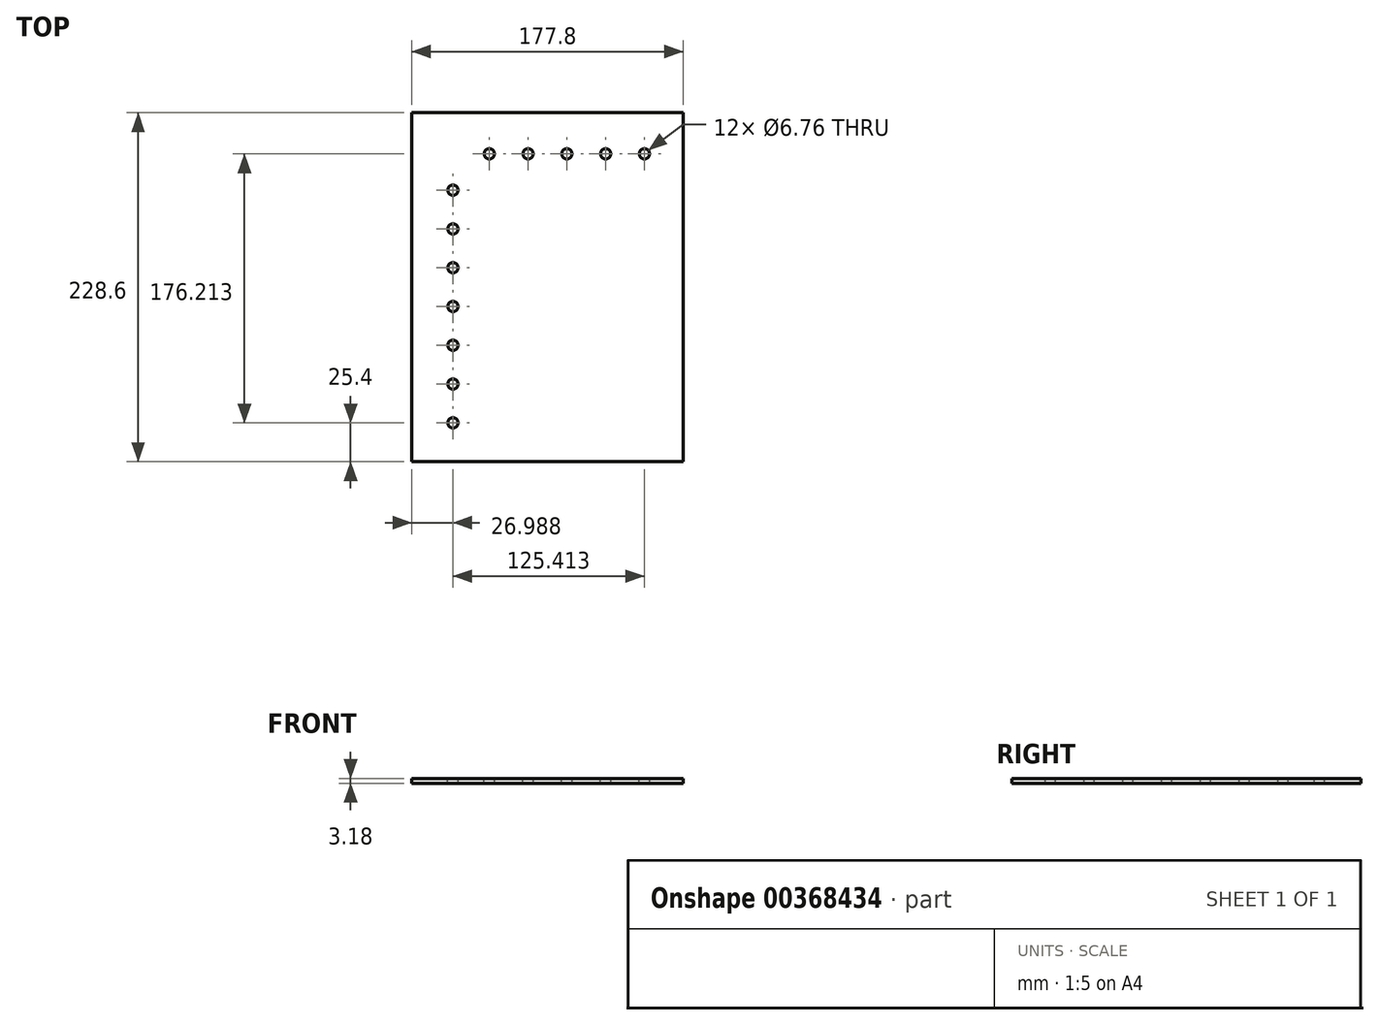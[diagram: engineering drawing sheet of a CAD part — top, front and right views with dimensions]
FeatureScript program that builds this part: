
annotation { "Feature Type Name" : "Feature", "Feature Type Description" : "" }
export const myFeature = defineFeature(function(context is Context, id is Id, definition is map)
    precondition{}
    {
        {
            var Q0;
            Q0=qCreatedBy(makeId("Top.planeOp"),FACE);
            var sketch = newSketch(context, id + "F0", { "sketchPlane" : qUnion([Q0])});
            skLineSegment(sketch, "E0.bottom", {"start": v(0, 0) * mm, "end": v(50.8, 0) * mm});
            skLineSegment(sketch, "E0.top", {"start": v(0, 177.8) * mm, "end": v(50.8, 177.8) * mm});
            skLineSegment(sketch, "E0.left", {"start": v(0, 0) * mm, "end": v(0, 177.8) * mm});
            skLineSegment(sketch, "E0.right", {"start": v(50.8, 0) * mm, "end": v(50.8, 177.8) * mm});
            skLineSegment(sketch, "E1.bottom", {"start": v(0, 228.6) * mm, "end": v(177.8, 228.6) * mm});
            skLineSegment(sketch, "E1.top", {"start": v(0, 177.8) * mm, "end": v(177.8, 177.8) * mm});
            skLineSegment(sketch, "E1.left", {"start": v(0, 228.6) * mm, "end": v(0, 177.8) * mm});
            skLineSegment(sketch, "E1.right", {"start": v(177.8, 228.6) * mm, "end": v(177.8, 177.8) * mm});
            skSolve(sketch);
        }
        {
            var Q0;
            Q0=makeQuery(id+"F0.imprint","IMPRINT",FACE,{"disambiguationData":[TD([[makeQuery(id+"F0.imprint","IMPRINT",EDGE,{"derivedFrom":sQuery(id+"F0.wireOp",EDGE,"E1.bottom")}),-1.0]])]});
            var Q1;
            Q1=makeQuery(id+"F0.imprint","IMPRINT",FACE,{"disambiguationData":[TD([[makeQuery(id+"F0.imprint","IMPRINT",EDGE,{"derivedFrom":sQuery(id+"F0.wireOp",EDGE,"E0.bottom")}),1.0]])]});
            extrude(context, id + "F1", {"entities" : qUnion([Q0, Q1]), "depth" : 3.17 * mm});
        }
        {
            var Q0;
            Q0=makeQuery(id+"F1.opExtrude","CAP_FACE",FACE,{"disambiguationData":[OSD([sQuery(id+"F0.wireOp",EDGE,"E0.bottom"),sQuery(id+"F0.wireOp",EDGE,"E0.left"),sQuery(id+"F0.wireOp",EDGE,"E0.right"),sQuery(id+"F0.wireOp",EDGE,"E1.bottom"),sQuery(id+"F0.wireOp",EDGE,"E1.top"),sQuery(id+"F0.wireOp",EDGE,"E1.left"),sQuery(id+"F0.wireOp",EDGE,"E1.right")])],"isStart":false});
            var sketch = newSketch(context, id + "F2", { "sketchPlane" : qUnion([Q0])});
            skLineSegment(sketch, "E2.0.0", {"start": v(177.8, 228.6) * mm, "end": v(0, 228.6) * mm, "construction": true});
            skLineSegment(sketch, "E2.0.1", {"start": v(0, 228.6) * mm, "end": v(0, 0) * mm, "construction": true});
            skLineSegment(sketch, "E2.0.2", {"start": v(0, 0) * mm, "end": v(50.8, 0) * mm, "construction": true});
            skLineSegment(sketch, "E2.0.3", {"start": v(50.8, 0) * mm, "end": v(50.8, 177.8) * mm, "construction": true});
            skLineSegment(sketch, "E2.0.4", {"start": v(50.8, 177.8) * mm, "end": v(177.8, 177.8) * mm, "construction": true});
            skLineSegment(sketch, "E2.0.5", {"start": v(177.8, 177.8) * mm, "end": v(177.8, 228.6) * mm, "construction": true});
            skLineSegment(sketch, "E3.0", {"start": v(3.18, 225.43) * mm, "end": v(3.18, 0) * mm});
            skLineSegment(sketch, "E4.0", {"start": v(177.8, 225.43) * mm, "end": v(3.17, 225.43) * mm});
            skLineSegment(sketch, "E5", {"start": v(177.8, 225.43) * mm, "end": v(177.8, 228.6) * mm});
            skLineSegment(sketch, "E6", {"start": v(177.8, 228.6) * mm, "end": v(0, 228.6) * mm});
            skLineSegment(sketch, "E7", {"start": v(0, 228.6) * mm, "end": v(0, 0) * mm});
            skLineSegment(sketch, "E8", {"start": v(0, 0) * mm, "end": v(3.18, 0) * mm});
            skSolve(sketch);
        }
        {
            var Q0;
            Q0=makeQuery(id+"F2.imprint","IMPRINT",FACE,{"disambiguationData":[TD([[makeQuery(id+"F2.imprint","IMPRINT",EDGE,{"derivedFrom":sQuery(id+"F2.wireOp",EDGE,"E3.0")}),-1.0]])]});
            extrude(context, id + "F3", {"entities" : qUnion([Q0]), "operationType" : NewBodyOperationType.ADD, "depth" : 76.2 * mm});
        }
        {
            var Q0;
            Q0=makeQuery(id+"F3.opExtrude","CAP_FACE",FACE,{"disambiguationData":[OSD([sQuery(id+"F2.wireOp",EDGE,"E3.0"),sQuery(id+"F2.wireOp",EDGE,"E4.0"),sQuery(id+"F2.wireOp",EDGE,"E5"),sQuery(id+"F2.wireOp",EDGE,"E6"),sQuery(id+"F2.wireOp",EDGE,"E7"),sQuery(id+"F2.wireOp",EDGE,"E8")])],"isStart":false});
            var sketch = newSketch(context, id + "F4", { "sketchPlane" : qUnion([Q0])});
            skLineSegment(sketch, "E9.0.0", {"start": v(0, 228.6) * mm, "end": v(177.8, 228.6) * mm});
            skLineSegment(sketch, "E9.0.1", {"start": v(177.8, 228.6) * mm, "end": v(177.8, 177.8) * mm});
            skLineSegment(sketch, "E9.0.2", {"start": v(177.8, 177.8) * mm, "end": v(50.8, 177.8) * mm});
            skLineSegment(sketch, "E9.0.3", {"start": v(50.8, 177.8) * mm, "end": v(50.8, 0) * mm});
            skLineSegment(sketch, "E9.0.4", {"start": v(50.8, 0) * mm, "end": v(0, 0) * mm});
            skLineSegment(sketch, "E9.0.5", {"start": v(0, 0) * mm, "end": v(0, 228.6) * mm});
            skSolve(sketch);
        }
        {
            var Q0;
            {var subQ4=sQuery(id+"F4.wireOp",EDGE,"E9.0.0");Q0=makeQuery(id+"F4.imprint","IMPRINT",FACE,{"disambiguationData":[TD([[makeQuery(id+"F4.imprint","IMPRINT",EDGE,{"derivedFrom":subQ4}),-1.0]])]});}
            var Q1;
            {var subQ3=sQuery(id+"F4.wireOp",EDGE,"E9.0.2");Q1=makeQuery(id+"F4.imprint","IMPRINT",FACE,{"disambiguationData":[TD([[makeQuery(id+"F4.imprint","IMPRINT",EDGE,{"derivedFrom":subQ3}),-1.0]])]});}
            extrude(context, id + "F5", {"entities" : qUnion([Q0, Q1]), "operationType" : NewBodyOperationType.ADD, "depth" : 3.17 * mm});
        }
        {
            var Q0;
            Q0=makeQuery(id+"F5.opExtrude","CAP_FACE",FACE,{"disambiguationData":[OSD([sQuery(id+"F4.wireOp",EDGE,"E9.0.0"),sQuery(id+"F4.wireOp",EDGE,"E9.0.1"),sQuery(id+"F4.wireOp",EDGE,"E9.0.2"),sQuery(id+"F4.wireOp",EDGE,"E9.0.3"),sQuery(id+"F4.wireOp",EDGE,"E9.0.4"),sQuery(id+"F4.wireOp",EDGE,"E9.0.5")])],"isStart":false});
            var sketch = newSketch(context, id + "F6", { "sketchPlane" : qUnion([Q0])});
            skLineSegment(sketch, "E10.0.0", {"start": v(50.8, 177.8) * mm, "end": v(177.8, 177.8) * mm, "construction": true});
            skLineSegment(sketch, "E10.0.1", {"start": v(177.8, 177.8) * mm, "end": v(177.8, 228.6) * mm, "construction": true});
            skLineSegment(sketch, "E10.0.2", {"start": v(177.8, 228.6) * mm, "end": v(0, 228.6) * mm, "construction": true});
            skLineSegment(sketch, "E10.0.3", {"start": v(0, 228.6) * mm, "end": v(0, 0) * mm, "construction": true});
            skLineSegment(sketch, "E10.0.4", {"start": v(0, 0) * mm, "end": v(50.8, 0) * mm, "construction": true});
            skLineSegment(sketch, "E10.0.5", {"start": v(50.8, 0) * mm, "end": v(50.8, 177.8) * mm, "construction": true});
            skLineSegment(sketch, "E11.0.0", {"start": v(177.8, 177.8) * mm, "end": v(177.8, 225.43) * mm, "construction": true});
            skLineSegment(sketch, "E11.0.1", {"start": v(177.8, 225.43) * mm, "end": v(3.17, 225.43) * mm, "construction": true});
            skLineSegment(sketch, "E11.0.2", {"start": v(3.18, 225.43) * mm, "end": v(3.18, 0) * mm, "construction": true});
            skLineSegment(sketch, "E11.0.3", {"start": v(3.18, 0) * mm, "end": v(50.8, 0) * mm, "construction": true});
            skLineSegment(sketch, "E12", {"start": v(26.99, 0) * mm, "end": v(26.99, 201.61) * mm, "construction": true});
            skLineSegment(sketch, "E13", {"start": v(177.8, 201.61) * mm, "end": v(26.99, 201.61) * mm, "construction": true});
            skPoint(sketch, "E14", {"position": v(26.99, 25.4) * mm});
            skPoint(sketch, "E15", {"position": v(152.4, 201.61) * mm});
            skPoint(sketch, "E16.0.1.0", {"position": v(26.99, 50.8) * mm});
            skPoint(sketch, "E16.0.2.0", {"position": v(26.99, 76.2) * mm});
            skPoint(sketch, "E16.0.3.0", {"position": v(26.99, 101.6) * mm});
            skPoint(sketch, "E16.0.4.0", {"position": v(26.99, 127) * mm});
            skPoint(sketch, "E16.0.5.0", {"position": v(26.99, 152.4) * mm});
            skPoint(sketch, "E16.0.6.0", {"position": v(26.99, 177.8) * mm});
            skLineSegment(sketch, "E16.direction1", {"start": v(26.99, 25.4) * mm, "end": v(52.39, 25.4) * mm, "construction": true});
            skLineSegment(sketch, "E16.direction2", {"start": v(26.99, 25.4) * mm, "end": v(26.99, 50.8) * mm, "construction": true});
            skPoint(sketch, "E17.1.0.0", {"position": v(127, 201.61) * mm});
            skPoint(sketch, "E17.2.0.0", {"position": v(101.6, 201.61) * mm});
            skPoint(sketch, "E17.3.0.0", {"position": v(76.2, 201.61) * mm});
            skPoint(sketch, "E17.4.0.0", {"position": v(50.8, 201.61) * mm});
            skLineSegment(sketch, "E17.direction1", {"start": v(152.4, 201.61) * mm, "end": v(127, 201.61) * mm, "construction": true});
            skSolve(sketch);
        }
        {
            var Q0;
            Q0=sQuery(id+"F6.wireOp",VERTEX,"E14");
            var Q1;
            Q1=sQuery(id+"F6.wireOp",VERTEX,"E16.0.1.0");
            var Q2;
            Q2=sQuery(id+"F6.wireOp",VERTEX,"E16.0.2.0");
            var Q3;
            Q3=sQuery(id+"F6.wireOp",VERTEX,"E16.0.3.0");
            var Q4;
            Q4=sQuery(id+"F6.wireOp",VERTEX,"E16.0.4.0");
            var Q5;
            Q5=sQuery(id+"F6.wireOp",VERTEX,"E16.0.5.0");
            var Q6;
            Q6=sQuery(id+"F6.wireOp",VERTEX,"E16.0.6.0");
            var Q7;
            Q7=sQuery(id+"F6.wireOp",VERTEX,"E17.4.0.0");
            var Q8;
            Q8=sQuery(id+"F6.wireOp",VERTEX,"E17.3.0.0");
            var Q9;
            Q9=sQuery(id+"F6.wireOp",VERTEX,"E17.2.0.0");
            var Q10;
            Q10=sQuery(id+"F6.wireOp",VERTEX,"E17.1.0.0");
            var Q11;
            Q11=sQuery(id+"F6.wireOp",VERTEX,"E15");
            var Q12;
            Q12=makeQuery(id+"F1.opExtrude","SWEPT_BODY",BODY,{"disambiguationData":[OSD([sQuery(id+"F0.wireOp",EDGE,"E0.bottom"),sQuery(id+"F0.wireOp",EDGE,"E0.left"),sQuery(id+"F0.wireOp",EDGE,"E0.right"),sQuery(id+"F0.wireOp",EDGE,"E1.bottom"),sQuery(id+"F0.wireOp",EDGE,"E1.top"),sQuery(id+"F0.wireOp",EDGE,"E1.left"),sQuery(id+"F0.wireOp",EDGE,"E1.right")])]});
            hole(context, id + "F7", {"style" : HoleStyle.SIMPLE, "endStyle" : HoleEndStyle.BLIND, "standardTappedOrClearance" : lookupTablePath({ "standard" : "ANSI", "fit" : "Normal (ASME)", "size" : "1/4", "type" : "Clearance" }), "standardBlindInLast" : lookupTablePath({ "fit" : "Free", "standard" : "ANSI", "size" : "1/4", "type" : "Clearance" }), "holeDiameter" : 6.76 * mm, "holeDepth" : 29.2 * mm, "isTappedThrough" : true, "tappedDepth" : 25.4 * mm, "tapClearance" : 3, "locations" : qUnion([Q0, Q1, Q2, Q3, Q4, Q5, Q6, Q7, Q8, Q9, Q10, Q11]), "scope" : qUnion([Q12])});
        }
        {
            var Q0;
            Q0=makeQuery(id+"F5.opExtrude","CAP_FACE",FACE,{"disambiguationData":[OSD([sQuery(id+"F4.wireOp",EDGE,"E9.0.0"),sQuery(id+"F4.wireOp",EDGE,"E9.0.1"),sQuery(id+"F4.wireOp",EDGE,"E9.0.2"),sQuery(id+"F4.wireOp",EDGE,"E9.0.3"),sQuery(id+"F4.wireOp",EDGE,"E9.0.4"),sQuery(id+"F4.wireOp",EDGE,"E9.0.5")])],"isStart":false});
            var sketch = newSketch(context, id + "F8", { "sketchPlane" : qUnion([Q0])});
            skLineSegment(sketch, "E18", {"start": v(0, 0) * mm, "end": v(0, 228.6) * mm});
            skLineSegment(sketch, "E19", {"start": v(0, 228.6) * mm, "end": v(177.8, 228.6) * mm});
            skLineSegment(sketch, "E20", {"start": v(177.8, 228.6) * mm, "end": v(177.8, 0) * mm});
            skLineSegment(sketch, "E21", {"start": v(177.8, 0) * mm, "end": v(0, 0) * mm});
            skSolve(sketch);
        }
        {
            var Q0;
            {var subQ1=makeQuery(id+"F5.opExtrude","CAP_EDGE",EDGE,{"disambiguationData":[OSD([sQuery(id+"F4.wireOp",EDGE,"E9.0.2")])],"isStart":false});Q0=makeQuery(id+"F8.imprint","IMPRINT",FACE,{"disambiguationData":[TD([[makeQuery(id+"F8.imprint","IMPRINT",EDGE,{"derivedFrom":subQ1}),1.0]])]});}
            var Q1;
            {var subQ2=sQuery(id+"F8.wireOp",EDGE,"E18");Q1=makeQuery(id+"F8.imprint","IMPRINT",FACE,{"disambiguationData":[TD([[makeQuery(id+"F8.imprint","IMPRINT",EDGE,{"derivedFrom":subQ2}),1.0]])]});}
            extrude(context, id + "F9", {"entities" : qUnion([Q0, Q1]), "operationType" : NewBodyOperationType.ADD, "depth" : 3.17 * mm});
        }
        {
            var Q0;
            Q0=qCreatedBy(makeId("Top.planeOp"),FACE);
            var sketch = newSketch(context, id + "F10", { "sketchPlane" : qUnion([Q0])});
            skLineSegment(sketch, "E22.bottom", {"start": v(-43.5, -136.07) * mm, "end": v(203.6, -136.07) * mm});
            skLineSegment(sketch, "E22.top", {"start": v(-43.5, 287.89) * mm, "end": v(203.6, 287.89) * mm});
            skLineSegment(sketch, "E22.left", {"start": v(-43.5, -136.07) * mm, "end": v(-43.5, 287.89) * mm});
            skLineSegment(sketch, "E22.right", {"start": v(203.6, -136.07) * mm, "end": v(203.6, 287.89) * mm});
            skSolve(sketch);
        }
        {
            var Q0;
            Q0=makeQuery(id+"F10.imprint","IMPRINT",FACE,{"disambiguationData":[TD([[makeQuery(id+"F10.imprint","IMPRINT",EDGE,{"derivedFrom":sQuery(id+"F10.wireOp",EDGE,"E22.bottom")}),1.0]])]});
            var Q1;
            Q1=makeQuery(id+"F9.opExtrude","CAP_FACE",FACE,{"disambiguationData":[OSD([sQuery(id+"F7.hole-0.sketch.wireOp",EDGE,"core_line_2"),sQuery(id+"F7.hole-0.sketch.wireOp",EDGE,"core_line_3"),sQuery(id+"F7.hole-1.sketch.wireOp",EDGE,"core_line_2"),sQuery(id+"F7.hole-1.sketch.wireOp",EDGE,"core_line_3"),sQuery(id+"F7.hole-2.sketch.wireOp",EDGE,"core_line_2"),sQuery(id+"F7.hole-2.sketch.wireOp",EDGE,"core_line_3"),sQuery(id+"F7.hole-3.sketch.wireOp",EDGE,"core_line_2"),sQuery(id+"F7.hole-3.sketch.wireOp",EDGE,"core_line_3"),sQuery(id+"F7.hole-4.sketch.wireOp",EDGE,"core_line_2"),sQuery(id+"F7.hole-4.sketch.wireOp",EDGE,"core_line_3"),sQuery(id+"F7.hole-5.sketch.wireOp",EDGE,"core_line_2"),sQuery(id+"F7.hole-5.sketch.wireOp",EDGE,"core_line_3"),sQuery(id+"F7.hole-6.sketch.wireOp",EDGE,"core_line_2"),sQuery(id+"F7.hole-6.sketch.wireOp",EDGE,"core_line_3"),sQuery(id+"F7.hole-7.sketch.wireOp",EDGE,"core_line_2"),sQuery(id+"F7.hole-7.sketch.wireOp",EDGE,"core_line_3"),sQuery(id+"F7.hole-8.sketch.wireOp",EDGE,"core_line_2"),sQuery(id+"F7.hole-8.sketch.wireOp",EDGE,"core_line_3"),sQuery(id+"F7.hole-9.sketch.wireOp",EDGE,"core_line_2"),sQuery(id+"F7.hole-9.sketch.wireOp",EDGE,"core_line_3"),sQuery(id+"F7.hole-10.sketch.wireOp",EDGE,"core_line_2"),sQuery(id+"F7.hole-10.sketch.wireOp",EDGE,"core_line_3"),sQuery(id+"F7.hole-11.sketch.wireOp",EDGE,"core_line_2"),sQuery(id+"F7.hole-11.sketch.wireOp",EDGE,"core_line_3"),sQuery(id+"F8.wireOp",EDGE,"E18"),sQuery(id+"F8.wireOp",EDGE,"E19"),sQuery(id+"F8.wireOp",EDGE,"E20"),sQuery(id+"F8.wireOp",EDGE,"E21")])],"isStart":true});
            extrude(context, id + "F11", {"entities" : qUnion([Q0]), "operationType" : NewBodyOperationType.REMOVE, "endBound" : BoundingType.UP_TO_SURFACE, "endBoundEntityFace" : qUnion([Q1]), "depth" : 25.4 * mm});
        }
    });
